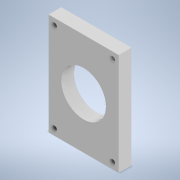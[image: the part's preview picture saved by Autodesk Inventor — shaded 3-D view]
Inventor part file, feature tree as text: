
AUTODESK INVENTOR PART (.ipt)
format: ipt  version: 2020 (Build 240168000, 168)  size: 122,880 bytes
history: native  units: in
note: dims shown in document units (in); Inventor stores cm internally (conversion verified against a paired STEP export)
features: other x4, reference x2, extrude x1, plane x1, sketch x1
ambient origin geometry x8: Origin, YZ Plane, XZ Plane, XY Plane, X Axis, Y Axis, Z Axis, Center Point
bodies: Solid1 (feature_tree)
feature tree (9):
  extrude  "Extrusion1"  Depth=0.5in TaperAngle=0.0deg
  plane  "Work Plane1"
  sketch  "Sketch1"  dims[d0=1.75in d1=0.5in d2=0.0in]
  reference  "Reference1"
  reference  "Reference2"
  other  "<userpath>\Desktop\PnP Machine\PnP Machine.iam"
  other  "PnP Machine.iam"
  other  "Stepper Standoff:1"
  other  "Stepper Standoff:2"
